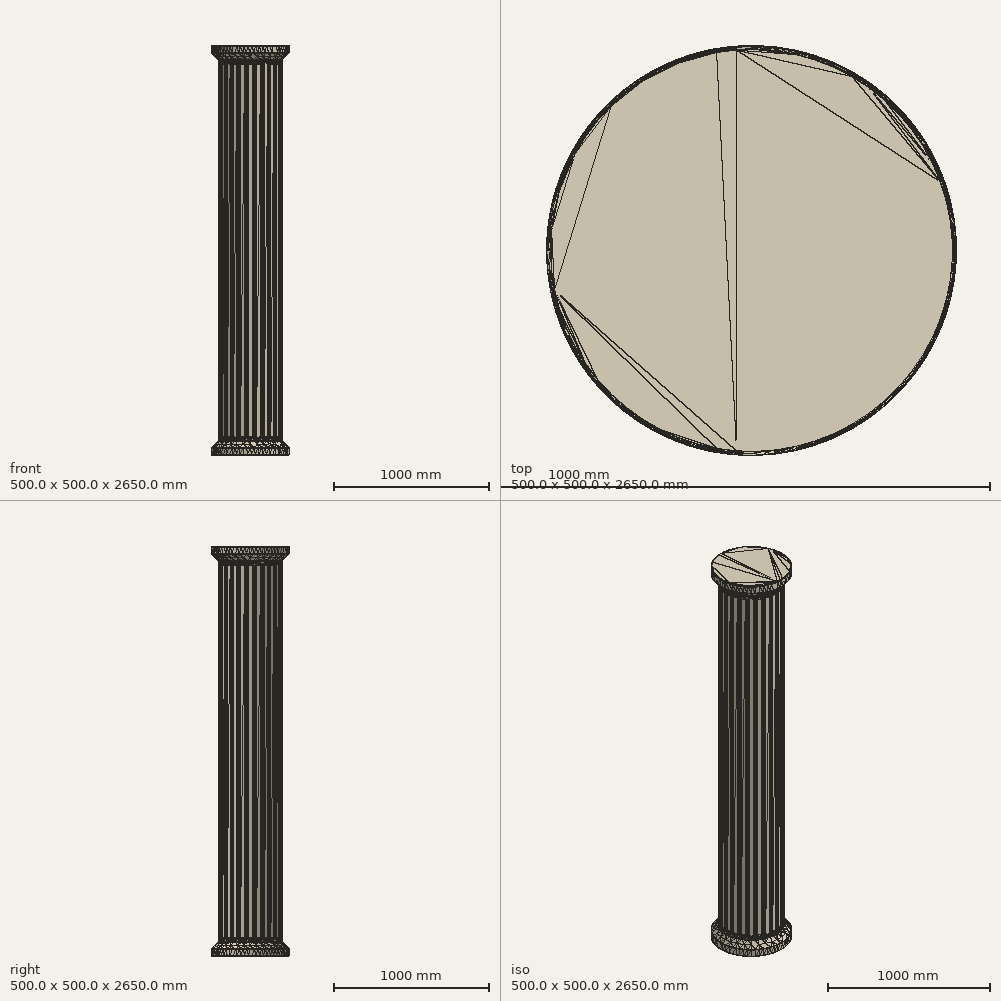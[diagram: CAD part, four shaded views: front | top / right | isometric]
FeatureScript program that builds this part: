
annotation { "Feature Type Name" : "Feature", "Feature Type Description" : "" }
export const myFeature = defineFeature(function(context is Context, id is Id, definition is map)
    precondition{}
    {
        {
            var Q0;
            Q0=qCreatedBy(makeId("Front.planeOp"),FACE);
            var sketch = newSketch(context, id + "F0", { "sketchPlane" : qUnion([Q0])});
            skLineSegment(sketch, "E0", {"start": v(0, 0) * mm, "end": v(250, 0) * mm});
            skLineSegment(sketch, "E1", {"start": v(250, 0) * mm, "end": v(250, 50) * mm});
            skLineSegment(sketch, "E2", {"start": v(250, 50) * mm, "end": v(206, 50) * mm});
            skLineSegment(sketch, "E3", {"start": v(206, 50) * mm, "end": v(206, 94) * mm});
            skLineSegment(sketch, "E4", {"start": v(206, 94) * mm, "end": v(250, 50) * mm});
            skLineSegment(sketch, "E5", {"start": v(0, 0) * mm, "end": v(0, 2650) * mm});
            skLineSegment(sketch, "E6", {"start": v(0, 2650) * mm, "end": v(250, 2650) * mm});
            skLineSegment(sketch, "E7", {"start": v(250, 2650) * mm, "end": v(250, 2600) * mm});
            skLineSegment(sketch, "E8", {"start": v(250, 2600) * mm, "end": v(206, 2600) * mm});
            skLineSegment(sketch, "E9", {"start": v(206, 2600) * mm, "end": v(206, 2556) * mm});
            skLineSegment(sketch, "E10", {"start": v(206, 2556) * mm, "end": v(250, 2600) * mm});
            skLineSegment(sketch, "E11", {"start": v(206, 2556) * mm, "end": v(206, 94) * mm});
            skLineSegment(sketch, "E12", {"start": v(206, 94) * mm, "end": v(0, 94) * mm});
            skSolve(sketch);
        }
        {
            var Q0;
            Q0 = qSketchRegion(id + "F0", true);
            var Q1;
            Q1=sQuery(id+"F0.wireOp",EDGE,"E5");
            revolve(context, id + "F1", {"surfaceOperationType" : NewSurfaceOperationType.NEW, "entities" : qUnion([Q0]), "axis" : qUnion([Q1]), "revolveType" : RevolveType.FULL});
        }
        {
            var Q0;
            Q0=qCreatedBy(makeId("Front.planeOp"),FACE);
            var sketch = newSketch(context, id + "F2", { "sketchPlane" : qUnion([Q0])});
            skLineSegment(sketch, "E13", {"start": v(0, 0) * mm, "end": v(0, 125) * mm});
            skLineSegment(sketch, "E14", {"start": v(0, 125) * mm, "end": v(10, 125) * mm});
            skLineSegment(sketch, "E15", {"start": v(10, 125) * mm, "end": v(10, 2525) * mm});
            skLineSegment(sketch, "E16", {"start": v(10, 2525) * mm, "end": v(-10, 2525) * mm});
            skLineSegment(sketch, "E17", {"start": v(-10, 2525) * mm, "end": v(-10, 125) * mm});
            skLineSegment(sketch, "E18", {"start": v(-10, 125) * mm, "end": v(0, 125) * mm});
            skArc(sketch, "E19", {"start": v(10, 2525) * mm, "mid": v(0, 2535) * mm, "end": v(-10, 2525) * mm});
            skArc(sketch, "E20", {"start": v(-10, 125) * mm, "mid": v(0, 115) * mm, "end": v(10, 125) * mm});
            skSolve(sketch);
        }
        {
            var Q0;
            Q0 = qSketchRegion(id + "F2", true);
            var Q1;
            Q1=makeQuery(id+"F1.opRevolve","SWEPT_FACE",FACE,{"disambiguationData":[OSD([sQuery(id+"F0.wireOp",EDGE,"E11")])]});
            extrude(context, id + "F3", {"entities" : qUnion([Q0]), "depth" : 210 * mm, "endBoundEntityFace" : qUnion([Q1]), "offsetDistance" : 25 * mm, "hasSecondDirection" : true, "secondDirectionOppositeDirection" : false, "secondDirectionDepth" : 200 * mm});
        }
        {
            var Q0;
            Q0=makeQuery(id+"F3.opExtrude","SWEPT_BODY",BODY,{"disambiguationData":[OSD([sQuery(id+"F2.wireOp",EDGE,"E15"),sQuery(id+"F2.wireOp",EDGE,"E17"),sQuery(id+"F2.wireOp",EDGE,"a2QfBqkh-tEiW-pIgy-MNU3-fEb1ejPm5M3t"),sQuery(id+"F2.wireOp",EDGE,"E19")])]});
            var Q1;
            Q1=sQuery(id+"F2.wireOp",EDGE,"E13");
            circularPattern(context, id + "F4", {"operationType" : NewBodyOperationType.REMOVE, "entities" : qUnion([Q0]), "axis" : qUnion([Q1]), "angle" : 360 * degree, "instanceCount" : 24, "equalSpace" : true});
        }
        {
            var Q0;
            Q0=makeQuery(id+"F4.boolean.opBoolean","INTERSECT",EDGE,{"derivedFrom":[makeQuery(id+"F1.opRevolve","SWEPT_FACE",FACE,{"disambiguationData":[OSD([sQuery(id+"F0.wireOp",EDGE,"E11")])]}),makeQuery(id+"F4.opPattern","COPY",FACE,{"derivedFrom":makeQuery(id+"F3.opExtrude","SWEPT_FACE",FACE,{"disambiguationData":[OSD([sQuery(id+"F2.wireOp",EDGE,"E17")])]}),"instanceName":"5"})]});
            var Q1;
            Q1=makeQuery(id+"F4.boolean.opBoolean","INTERSECT",EDGE,{"derivedFrom":[makeQuery(id+"F1.opRevolve","SWEPT_FACE",FACE,{"disambiguationData":[OSD([sQuery(id+"F0.wireOp",EDGE,"E11")])]}),makeQuery(id+"F4.opPattern","COPY",FACE,{"derivedFrom":makeQuery(id+"F3.opExtrude","SWEPT_FACE",FACE,{"disambiguationData":[OSD([sQuery(id+"F2.wireOp",EDGE,"E17")])]}),"instanceName":"6"})]});
            var Q2;
            Q2=makeQuery(id+"F4.boolean.opBoolean","INTERSECT",EDGE,{"derivedFrom":[makeQuery(id+"F1.opRevolve","SWEPT_FACE",FACE,{"disambiguationData":[OSD([sQuery(id+"F0.wireOp",EDGE,"E11")])]}),makeQuery(id+"F4.opPattern","COPY",FACE,{"derivedFrom":makeQuery(id+"F3.opExtrude","SWEPT_FACE",FACE,{"disambiguationData":[OSD([sQuery(id+"F2.wireOp",EDGE,"E17")])]}),"instanceName":"7"})]});
            var Q3;
            Q3=makeQuery(id+"F4.boolean.opBoolean","INTERSECT",EDGE,{"derivedFrom":[makeQuery(id+"F1.opRevolve","SWEPT_FACE",FACE,{"disambiguationData":[OSD([sQuery(id+"F0.wireOp",EDGE,"E11")])]}),makeQuery(id+"F4.opPattern","COPY",FACE,{"derivedFrom":makeQuery(id+"F3.opExtrude","SWEPT_FACE",FACE,{"disambiguationData":[OSD([sQuery(id+"F2.wireOp",EDGE,"E17")])]}),"instanceName":"8"})]});
            var Q4;
            Q4=makeQuery(id+"F4.boolean.opBoolean","INTERSECT",EDGE,{"derivedFrom":[makeQuery(id+"F1.opRevolve","SWEPT_FACE",FACE,{"disambiguationData":[OSD([sQuery(id+"F0.wireOp",EDGE,"E11")])]}),makeQuery(id+"F4.opPattern","COPY",FACE,{"derivedFrom":makeQuery(id+"F3.opExtrude","SWEPT_FACE",FACE,{"disambiguationData":[OSD([sQuery(id+"F2.wireOp",EDGE,"E17")])]}),"instanceName":"9"})]});
            var Q5;
            Q5=makeQuery(id+"F4.boolean.opBoolean","INTERSECT",EDGE,{"derivedFrom":[makeQuery(id+"F1.opRevolve","SWEPT_FACE",FACE,{"disambiguationData":[OSD([sQuery(id+"F0.wireOp",EDGE,"E11")])]}),makeQuery(id+"F4.opPattern","COPY",FACE,{"derivedFrom":makeQuery(id+"F3.opExtrude","SWEPT_FACE",FACE,{"disambiguationData":[OSD([sQuery(id+"F2.wireOp",EDGE,"E17")])]}),"instanceName":"10"})]});
            var Q6;
            Q6=makeQuery(id+"F4.boolean.opBoolean","INTERSECT",EDGE,{"derivedFrom":[makeQuery(id+"F1.opRevolve","SWEPT_FACE",FACE,{"disambiguationData":[OSD([sQuery(id+"F0.wireOp",EDGE,"E11")])]}),makeQuery(id+"F4.opPattern","COPY",FACE,{"derivedFrom":makeQuery(id+"F3.opExtrude","SWEPT_FACE",FACE,{"disambiguationData":[OSD([sQuery(id+"F2.wireOp",EDGE,"E17")])]}),"instanceName":"11"})]});
            var Q7;
            Q7=makeQuery(id+"F4.boolean.opBoolean","INTERSECT",EDGE,{"derivedFrom":[makeQuery(id+"F1.opRevolve","SWEPT_FACE",FACE,{"disambiguationData":[OSD([sQuery(id+"F0.wireOp",EDGE,"E11")])]}),makeQuery(id+"F4.opPattern","COPY",FACE,{"derivedFrom":makeQuery(id+"F3.opExtrude","SWEPT_FACE",FACE,{"disambiguationData":[OSD([sQuery(id+"F2.wireOp",EDGE,"E17")])]}),"instanceName":"12"})]});
            var Q8;
            Q8=makeQuery(id+"F4.boolean.opBoolean","INTERSECT",EDGE,{"derivedFrom":[makeQuery(id+"F1.opRevolve","SWEPT_FACE",FACE,{"disambiguationData":[OSD([sQuery(id+"F0.wireOp",EDGE,"E11")])]}),makeQuery(id+"F4.opPattern","COPY",FACE,{"derivedFrom":makeQuery(id+"F3.opExtrude","SWEPT_FACE",FACE,{"disambiguationData":[OSD([sQuery(id+"F2.wireOp",EDGE,"E17")])]}),"instanceName":"13"})]});
            var Q9;
            Q9=makeQuery(id+"F4.boolean.opBoolean","INTERSECT",EDGE,{"derivedFrom":[makeQuery(id+"F1.opRevolve","SWEPT_FACE",FACE,{"disambiguationData":[OSD([sQuery(id+"F0.wireOp",EDGE,"E11")])]}),makeQuery(id+"F4.opPattern","COPY",FACE,{"derivedFrom":makeQuery(id+"F3.opExtrude","SWEPT_FACE",FACE,{"disambiguationData":[OSD([sQuery(id+"F2.wireOp",EDGE,"E17")])]}),"instanceName":"14"})]});
            var Q10;
            Q10=makeQuery(id+"F4.boolean.opBoolean","INTERSECT",EDGE,{"derivedFrom":[makeQuery(id+"F1.opRevolve","SWEPT_FACE",FACE,{"disambiguationData":[OSD([sQuery(id+"F0.wireOp",EDGE,"E11")])]}),makeQuery(id+"F4.opPattern","COPY",FACE,{"derivedFrom":makeQuery(id+"F3.opExtrude","SWEPT_FACE",FACE,{"disambiguationData":[OSD([sQuery(id+"F2.wireOp",EDGE,"E17")])]}),"instanceName":"15"})]});
            var Q11;
            Q11=makeQuery(id+"F4.boolean.opBoolean","INTERSECT",EDGE,{"derivedFrom":[makeQuery(id+"F1.opRevolve","SWEPT_FACE",FACE,{"disambiguationData":[OSD([sQuery(id+"F0.wireOp",EDGE,"E11")])]}),makeQuery(id+"F4.opPattern","COPY",FACE,{"derivedFrom":makeQuery(id+"F3.opExtrude","SWEPT_FACE",FACE,{"disambiguationData":[OSD([sQuery(id+"F2.wireOp",EDGE,"E17")])]}),"instanceName":"16"})]});
            var Q12;
            Q12=makeQuery(id+"F4.boolean.opBoolean","INTERSECT",EDGE,{"derivedFrom":[makeQuery(id+"F1.opRevolve","SWEPT_FACE",FACE,{"disambiguationData":[OSD([sQuery(id+"F0.wireOp",EDGE,"E11")])]}),makeQuery(id+"F4.opPattern","COPY",FACE,{"derivedFrom":makeQuery(id+"F3.opExtrude","SWEPT_FACE",FACE,{"disambiguationData":[OSD([sQuery(id+"F2.wireOp",EDGE,"E17")])]}),"instanceName":"17"})]});
            var Q13;
            Q13=makeQuery(id+"F4.boolean.opBoolean","INTERSECT",EDGE,{"derivedFrom":[makeQuery(id+"F1.opRevolve","SWEPT_FACE",FACE,{"disambiguationData":[OSD([sQuery(id+"F0.wireOp",EDGE,"E11")])]}),makeQuery(id+"F4.opPattern","COPY",FACE,{"derivedFrom":makeQuery(id+"F3.opExtrude","SWEPT_FACE",FACE,{"disambiguationData":[OSD([sQuery(id+"F2.wireOp",EDGE,"E17")])]}),"instanceName":"18"})]});
            var Q14;
            Q14=makeQuery(id+"F4.boolean.opBoolean","INTERSECT",EDGE,{"derivedFrom":[makeQuery(id+"F1.opRevolve","SWEPT_FACE",FACE,{"disambiguationData":[OSD([sQuery(id+"F0.wireOp",EDGE,"E11")])]}),makeQuery(id+"F4.opPattern","COPY",FACE,{"derivedFrom":makeQuery(id+"F3.opExtrude","SWEPT_FACE",FACE,{"disambiguationData":[OSD([sQuery(id+"F2.wireOp",EDGE,"E17")])]}),"instanceName":"19"})]});
            var Q15;
            Q15=makeQuery(id+"F4.boolean.opBoolean","INTERSECT",EDGE,{"derivedFrom":[makeQuery(id+"F1.opRevolve","SWEPT_FACE",FACE,{"disambiguationData":[OSD([sQuery(id+"F0.wireOp",EDGE,"E11")])]}),makeQuery(id+"F4.opPattern","COPY",FACE,{"derivedFrom":makeQuery(id+"F3.opExtrude","SWEPT_FACE",FACE,{"disambiguationData":[OSD([sQuery(id+"F2.wireOp",EDGE,"E17")])]}),"instanceName":"20"})]});
            var Q16;
            Q16=makeQuery(id+"F4.boolean.opBoolean","INTERSECT",EDGE,{"derivedFrom":[makeQuery(id+"F1.opRevolve","SWEPT_FACE",FACE,{"disambiguationData":[OSD([sQuery(id+"F0.wireOp",EDGE,"E11")])]}),makeQuery(id+"F4.opPattern","COPY",FACE,{"derivedFrom":makeQuery(id+"F3.opExtrude","SWEPT_FACE",FACE,{"disambiguationData":[OSD([sQuery(id+"F2.wireOp",EDGE,"E17")])]}),"instanceName":"21"})]});
            var Q17;
            Q17=makeQuery(id+"F4.boolean.opBoolean","INTERSECT",EDGE,{"derivedFrom":[makeQuery(id+"F1.opRevolve","SWEPT_FACE",FACE,{"disambiguationData":[OSD([sQuery(id+"F0.wireOp",EDGE,"E11")])]}),makeQuery(id+"F4.opPattern","COPY",FACE,{"derivedFrom":makeQuery(id+"F3.opExtrude","SWEPT_FACE",FACE,{"disambiguationData":[OSD([sQuery(id+"F2.wireOp",EDGE,"E17")])]}),"instanceName":"22"})]});
            var Q18;
            Q18=makeQuery(id+"F4.boolean.opBoolean","INTERSECT",EDGE,{"derivedFrom":[makeQuery(id+"F1.opRevolve","SWEPT_FACE",FACE,{"disambiguationData":[OSD([sQuery(id+"F0.wireOp",EDGE,"E11")])]}),makeQuery(id+"F4.opPattern","COPY",FACE,{"derivedFrom":makeQuery(id+"F3.opExtrude","SWEPT_FACE",FACE,{"disambiguationData":[OSD([sQuery(id+"F2.wireOp",EDGE,"E17")])]}),"instanceName":"23"})]});
            var Q19;
            Q19=makeQuery(id+"F4.boolean.opBoolean","INTERSECT",EDGE,{"derivedFrom":[makeQuery(id+"F1.opRevolve","SWEPT_FACE",FACE,{"disambiguationData":[OSD([sQuery(id+"F0.wireOp",EDGE,"E11")])]}),makeQuery(id+"F3.opExtrude","SWEPT_FACE",FACE,{"disambiguationData":[OSD([sQuery(id+"F2.wireOp",EDGE,"E17")])]})]});
            var Q20;
            Q20=makeQuery(id+"F4.boolean.opBoolean","INTERSECT",EDGE,{"derivedFrom":[makeQuery(id+"F1.opRevolve","SWEPT_FACE",FACE,{"disambiguationData":[OSD([sQuery(id+"F0.wireOp",EDGE,"E11")])]}),makeQuery(id+"F4.opPattern","COPY",FACE,{"derivedFrom":makeQuery(id+"F3.opExtrude","SWEPT_FACE",FACE,{"disambiguationData":[OSD([sQuery(id+"F2.wireOp",EDGE,"E17")])]}),"instanceName":"1"})]});
            var Q21;
            Q21=makeQuery(id+"F4.boolean.opBoolean","INTERSECT",EDGE,{"derivedFrom":[makeQuery(id+"F1.opRevolve","SWEPT_FACE",FACE,{"disambiguationData":[OSD([sQuery(id+"F0.wireOp",EDGE,"E11")])]}),makeQuery(id+"F4.opPattern","COPY",FACE,{"derivedFrom":makeQuery(id+"F3.opExtrude","SWEPT_FACE",FACE,{"disambiguationData":[OSD([sQuery(id+"F2.wireOp",EDGE,"E17")])]}),"instanceName":"2"})]});
            var Q22;
            Q22=makeQuery(id+"F4.boolean.opBoolean","INTERSECT",EDGE,{"derivedFrom":[makeQuery(id+"F1.opRevolve","SWEPT_FACE",FACE,{"disambiguationData":[OSD([sQuery(id+"F0.wireOp",EDGE,"E11")])]}),makeQuery(id+"F4.opPattern","COPY",FACE,{"derivedFrom":makeQuery(id+"F3.opExtrude","SWEPT_FACE",FACE,{"disambiguationData":[OSD([sQuery(id+"F2.wireOp",EDGE,"E17")])]}),"instanceName":"3"})]});
            var Q23;
            Q23=makeQuery(id+"F4.boolean.opBoolean","INTERSECT",EDGE,{"derivedFrom":[makeQuery(id+"F1.opRevolve","SWEPT_FACE",FACE,{"disambiguationData":[OSD([sQuery(id+"F0.wireOp",EDGE,"E11")])]}),makeQuery(id+"F4.opPattern","COPY",FACE,{"derivedFrom":makeQuery(id+"F3.opExtrude","SWEPT_FACE",FACE,{"disambiguationData":[OSD([sQuery(id+"F2.wireOp",EDGE,"E17")])]}),"instanceName":"4"})]});
            chamfer(context, id + "F5", {"entities" : qUnion([Q0, Q1, Q2, Q3, Q4, Q5, Q6, Q7, Q8, Q9, Q10, Q11, Q12, Q13, Q14, Q15, Q16, Q17, Q18, Q19, Q20, Q21, Q22, Q23]), "width" : 10 * mm, "tangentPropagation" : true});
        }
        {
            var Q0;
            Q0=makeQuery(id+"F1.opRevolve","SWEPT_EDGE",EDGE,{"disambiguationData":[OSD([sQuery(id+"F0.wireOp",EDGE,"E6"),sQuery(id+"F0.wireOp",EDGE,"E7")])]});
            var Q1;
            Q1=makeQuery(id+"F1.opRevolve","SWEPT_EDGE",EDGE,{"disambiguationData":[OSD([sQuery(id+"F0.wireOp",EDGE,"E7"),sQuery(id+"F0.wireOp",EDGE,"E8"),sQuery(id+"F0.wireOp",EDGE,"E10")])]});
            var Q2;
            Q2=makeQuery(id+"F1.opRevolve","SWEPT_EDGE",EDGE,{"disambiguationData":[OSD([sQuery(id+"F0.wireOp",EDGE,"E9"),sQuery(id+"F0.wireOp",EDGE,"E10"),sQuery(id+"F0.wireOp",EDGE,"E11")])]});
            var Q3;
            Q3=makeQuery(id+"F1.opRevolve","SWEPT_EDGE",EDGE,{"disambiguationData":[OSD([sQuery(id+"F0.wireOp",EDGE,"E0"),sQuery(id+"F0.wireOp",EDGE,"E1")])]});
            var Q4;
            Q4=makeQuery(id+"F1.opRevolve","SWEPT_EDGE",EDGE,{"disambiguationData":[OSD([sQuery(id+"F0.wireOp",EDGE,"E1"),sQuery(id+"F0.wireOp",EDGE,"E2"),sQuery(id+"F0.wireOp",EDGE,"E4")])]});
            var Q5;
            Q5=makeQuery(id+"F1.opRevolve","SWEPT_EDGE",EDGE,{"disambiguationData":[OSD([sQuery(id+"F0.wireOp",EDGE,"E3"),sQuery(id+"F0.wireOp",EDGE,"E4"),sQuery(id+"F0.wireOp",EDGE,"E11"),sQuery(id+"F0.wireOp",EDGE,"E12")])]});
            var Q6;
            Q6=makeQuery(id+"F4.boolean.opBoolean","COPY",FACE,{"derivedFrom":makeQuery(id+"F4.opPattern","COPY",FACE,{"derivedFrom":makeQuery(id+"F3.opExtrude","CAP_FACE",FACE,{"disambiguationData":[OSD([sQuery(id+"F2.wireOp",EDGE,"E15"),sQuery(id+"F2.wireOp",EDGE,"E17"),sQuery(id+"F2.wireOp",EDGE,"E19"),sQuery(id+"F2.wireOp",EDGE,"E20")])],"isStart":true}),"instanceName":"3"})});
            var Q7;
            Q7=makeQuery(id+"F4.boolean.opBoolean","COPY",FACE,{"derivedFrom":makeQuery(id+"F4.opPattern","COPY",FACE,{"derivedFrom":makeQuery(id+"F3.opExtrude","CAP_FACE",FACE,{"disambiguationData":[OSD([sQuery(id+"F2.wireOp",EDGE,"E15"),sQuery(id+"F2.wireOp",EDGE,"E17"),sQuery(id+"F2.wireOp",EDGE,"E19"),sQuery(id+"F2.wireOp",EDGE,"E20")])],"isStart":true}),"instanceName":"4"})});
            var Q8;
            Q8=makeQuery(id+"F4.boolean.opBoolean","COPY",FACE,{"derivedFrom":makeQuery(id+"F4.opPattern","COPY",FACE,{"derivedFrom":makeQuery(id+"F3.opExtrude","CAP_FACE",FACE,{"disambiguationData":[OSD([sQuery(id+"F2.wireOp",EDGE,"E15"),sQuery(id+"F2.wireOp",EDGE,"E17"),sQuery(id+"F2.wireOp",EDGE,"E19"),sQuery(id+"F2.wireOp",EDGE,"E20")])],"isStart":true}),"instanceName":"5"})});
            var Q9;
            Q9=makeQuery(id+"F4.boolean.opBoolean","COPY",FACE,{"derivedFrom":makeQuery(id+"F4.opPattern","COPY",FACE,{"derivedFrom":makeQuery(id+"F3.opExtrude","CAP_FACE",FACE,{"disambiguationData":[OSD([sQuery(id+"F2.wireOp",EDGE,"E15"),sQuery(id+"F2.wireOp",EDGE,"E17"),sQuery(id+"F2.wireOp",EDGE,"E19"),sQuery(id+"F2.wireOp",EDGE,"E20")])],"isStart":true}),"instanceName":"6"})});
            var Q10;
            Q10=makeQuery(id+"F4.boolean.opBoolean","COPY",FACE,{"derivedFrom":makeQuery(id+"F4.opPattern","COPY",FACE,{"derivedFrom":makeQuery(id+"F3.opExtrude","CAP_FACE",FACE,{"disambiguationData":[OSD([sQuery(id+"F2.wireOp",EDGE,"E15"),sQuery(id+"F2.wireOp",EDGE,"E17"),sQuery(id+"F2.wireOp",EDGE,"E19"),sQuery(id+"F2.wireOp",EDGE,"E20")])],"isStart":true}),"instanceName":"7"})});
            var Q11;
            Q11=makeQuery(id+"F4.boolean.opBoolean","COPY",FACE,{"derivedFrom":makeQuery(id+"F4.opPattern","COPY",FACE,{"derivedFrom":makeQuery(id+"F3.opExtrude","CAP_FACE",FACE,{"disambiguationData":[OSD([sQuery(id+"F2.wireOp",EDGE,"E15"),sQuery(id+"F2.wireOp",EDGE,"E17"),sQuery(id+"F2.wireOp",EDGE,"E19"),sQuery(id+"F2.wireOp",EDGE,"E20")])],"isStart":true}),"instanceName":"8"})});
            var Q12;
            Q12=makeQuery(id+"F4.boolean.opBoolean","COPY",FACE,{"derivedFrom":makeQuery(id+"F4.opPattern","COPY",FACE,{"derivedFrom":makeQuery(id+"F3.opExtrude","CAP_FACE",FACE,{"disambiguationData":[OSD([sQuery(id+"F2.wireOp",EDGE,"E15"),sQuery(id+"F2.wireOp",EDGE,"E17"),sQuery(id+"F2.wireOp",EDGE,"E19"),sQuery(id+"F2.wireOp",EDGE,"E20")])],"isStart":true}),"instanceName":"9"})});
            var Q13;
            Q13=makeQuery(id+"F4.boolean.opBoolean","COPY",FACE,{"derivedFrom":makeQuery(id+"F4.opPattern","COPY",FACE,{"derivedFrom":makeQuery(id+"F3.opExtrude","CAP_FACE",FACE,{"disambiguationData":[OSD([sQuery(id+"F2.wireOp",EDGE,"E15"),sQuery(id+"F2.wireOp",EDGE,"E17"),sQuery(id+"F2.wireOp",EDGE,"E19"),sQuery(id+"F2.wireOp",EDGE,"E20")])],"isStart":true}),"instanceName":"10"})});
            var Q14;
            Q14=makeQuery(id+"F4.boolean.opBoolean","COPY",FACE,{"derivedFrom":makeQuery(id+"F4.opPattern","COPY",FACE,{"derivedFrom":makeQuery(id+"F3.opExtrude","CAP_FACE",FACE,{"disambiguationData":[OSD([sQuery(id+"F2.wireOp",EDGE,"E15"),sQuery(id+"F2.wireOp",EDGE,"E17"),sQuery(id+"F2.wireOp",EDGE,"E19"),sQuery(id+"F2.wireOp",EDGE,"E20")])],"isStart":true}),"instanceName":"11"})});
            var Q15;
            Q15=makeQuery(id+"F4.boolean.opBoolean","COPY",FACE,{"derivedFrom":makeQuery(id+"F4.opPattern","COPY",FACE,{"derivedFrom":makeQuery(id+"F3.opExtrude","CAP_FACE",FACE,{"disambiguationData":[OSD([sQuery(id+"F2.wireOp",EDGE,"E15"),sQuery(id+"F2.wireOp",EDGE,"E17"),sQuery(id+"F2.wireOp",EDGE,"E19"),sQuery(id+"F2.wireOp",EDGE,"E20")])],"isStart":true}),"instanceName":"12"})});
            var Q16;
            Q16=makeQuery(id+"F4.boolean.opBoolean","COPY",FACE,{"derivedFrom":makeQuery(id+"F4.opPattern","COPY",FACE,{"derivedFrom":makeQuery(id+"F3.opExtrude","CAP_FACE",FACE,{"disambiguationData":[OSD([sQuery(id+"F2.wireOp",EDGE,"E15"),sQuery(id+"F2.wireOp",EDGE,"E17"),sQuery(id+"F2.wireOp",EDGE,"E19"),sQuery(id+"F2.wireOp",EDGE,"E20")])],"isStart":true}),"instanceName":"13"})});
            var Q17;
            Q17=makeQuery(id+"F4.boolean.opBoolean","COPY",FACE,{"derivedFrom":makeQuery(id+"F4.opPattern","COPY",FACE,{"derivedFrom":makeQuery(id+"F3.opExtrude","CAP_FACE",FACE,{"disambiguationData":[OSD([sQuery(id+"F2.wireOp",EDGE,"E15"),sQuery(id+"F2.wireOp",EDGE,"E17"),sQuery(id+"F2.wireOp",EDGE,"E19"),sQuery(id+"F2.wireOp",EDGE,"E20")])],"isStart":true}),"instanceName":"14"})});
            var Q18;
            Q18=makeQuery(id+"F4.boolean.opBoolean","COPY",FACE,{"derivedFrom":makeQuery(id+"F4.opPattern","COPY",FACE,{"derivedFrom":makeQuery(id+"F3.opExtrude","CAP_FACE",FACE,{"disambiguationData":[OSD([sQuery(id+"F2.wireOp",EDGE,"E15"),sQuery(id+"F2.wireOp",EDGE,"E17"),sQuery(id+"F2.wireOp",EDGE,"E19"),sQuery(id+"F2.wireOp",EDGE,"E20")])],"isStart":true}),"instanceName":"15"})});
            var Q19;
            Q19=makeQuery(id+"F4.boolean.opBoolean","COPY",FACE,{"derivedFrom":makeQuery(id+"F4.opPattern","COPY",FACE,{"derivedFrom":makeQuery(id+"F3.opExtrude","CAP_FACE",FACE,{"disambiguationData":[OSD([sQuery(id+"F2.wireOp",EDGE,"E15"),sQuery(id+"F2.wireOp",EDGE,"E17"),sQuery(id+"F2.wireOp",EDGE,"E19"),sQuery(id+"F2.wireOp",EDGE,"E20")])],"isStart":true}),"instanceName":"16"})});
            var Q20;
            Q20=makeQuery(id+"F4.boolean.opBoolean","COPY",FACE,{"derivedFrom":makeQuery(id+"F4.opPattern","COPY",FACE,{"derivedFrom":makeQuery(id+"F3.opExtrude","CAP_FACE",FACE,{"disambiguationData":[OSD([sQuery(id+"F2.wireOp",EDGE,"E15"),sQuery(id+"F2.wireOp",EDGE,"E17"),sQuery(id+"F2.wireOp",EDGE,"E19"),sQuery(id+"F2.wireOp",EDGE,"E20")])],"isStart":true}),"instanceName":"17"})});
            var Q21;
            Q21=makeQuery(id+"F4.boolean.opBoolean","COPY",FACE,{"derivedFrom":makeQuery(id+"F4.opPattern","COPY",FACE,{"derivedFrom":makeQuery(id+"F3.opExtrude","CAP_FACE",FACE,{"disambiguationData":[OSD([sQuery(id+"F2.wireOp",EDGE,"E15"),sQuery(id+"F2.wireOp",EDGE,"E17"),sQuery(id+"F2.wireOp",EDGE,"E19"),sQuery(id+"F2.wireOp",EDGE,"E20")])],"isStart":true}),"instanceName":"18"})});
            var Q22;
            Q22=makeQuery(id+"F4.boolean.opBoolean","COPY",FACE,{"derivedFrom":makeQuery(id+"F4.opPattern","COPY",FACE,{"derivedFrom":makeQuery(id+"F3.opExtrude","CAP_FACE",FACE,{"disambiguationData":[OSD([sQuery(id+"F2.wireOp",EDGE,"E15"),sQuery(id+"F2.wireOp",EDGE,"E17"),sQuery(id+"F2.wireOp",EDGE,"E19"),sQuery(id+"F2.wireOp",EDGE,"E20")])],"isStart":true}),"instanceName":"19"})});
            var Q23;
            Q23=makeQuery(id+"F4.boolean.opBoolean","COPY",FACE,{"derivedFrom":makeQuery(id+"F4.opPattern","COPY",FACE,{"derivedFrom":makeQuery(id+"F3.opExtrude","CAP_FACE",FACE,{"disambiguationData":[OSD([sQuery(id+"F2.wireOp",EDGE,"E15"),sQuery(id+"F2.wireOp",EDGE,"E17"),sQuery(id+"F2.wireOp",EDGE,"E19"),sQuery(id+"F2.wireOp",EDGE,"E20")])],"isStart":true}),"instanceName":"20"})});
            var Q24;
            Q24=makeQuery(id+"F4.boolean.opBoolean","COPY",FACE,{"derivedFrom":makeQuery(id+"F4.opPattern","COPY",FACE,{"derivedFrom":makeQuery(id+"F3.opExtrude","CAP_FACE",FACE,{"disambiguationData":[OSD([sQuery(id+"F2.wireOp",EDGE,"E15"),sQuery(id+"F2.wireOp",EDGE,"E17"),sQuery(id+"F2.wireOp",EDGE,"E19"),sQuery(id+"F2.wireOp",EDGE,"E20")])],"isStart":true}),"instanceName":"21"})});
            var Q25;
            Q25=makeQuery(id+"F4.boolean.opBoolean","COPY",FACE,{"derivedFrom":makeQuery(id+"F4.opPattern","COPY",FACE,{"derivedFrom":makeQuery(id+"F3.opExtrude","CAP_FACE",FACE,{"disambiguationData":[OSD([sQuery(id+"F2.wireOp",EDGE,"E15"),sQuery(id+"F2.wireOp",EDGE,"E17"),sQuery(id+"F2.wireOp",EDGE,"E19"),sQuery(id+"F2.wireOp",EDGE,"E20")])],"isStart":true}),"instanceName":"22"})});
            var Q26;
            Q26=makeQuery(id+"F4.boolean.opBoolean","COPY",FACE,{"derivedFrom":makeQuery(id+"F4.opPattern","COPY",FACE,{"derivedFrom":makeQuery(id+"F3.opExtrude","CAP_FACE",FACE,{"disambiguationData":[OSD([sQuery(id+"F2.wireOp",EDGE,"E15"),sQuery(id+"F2.wireOp",EDGE,"E17"),sQuery(id+"F2.wireOp",EDGE,"E19"),sQuery(id+"F2.wireOp",EDGE,"E20")])],"isStart":true}),"instanceName":"23"})});
            var Q27;
            Q27=makeQuery(id+"F4.boolean.opBoolean","COPY",FACE,{"derivedFrom":makeQuery(id+"F3.opExtrude","CAP_FACE",FACE,{"disambiguationData":[OSD([sQuery(id+"F2.wireOp",EDGE,"E15"),sQuery(id+"F2.wireOp",EDGE,"E17"),sQuery(id+"F2.wireOp",EDGE,"E19"),sQuery(id+"F2.wireOp",EDGE,"E20")])],"isStart":true})});
            var Q28;
            Q28=makeQuery(id+"F4.boolean.opBoolean","COPY",FACE,{"derivedFrom":makeQuery(id+"F4.opPattern","COPY",FACE,{"derivedFrom":makeQuery(id+"F3.opExtrude","CAP_FACE",FACE,{"disambiguationData":[OSD([sQuery(id+"F2.wireOp",EDGE,"E15"),sQuery(id+"F2.wireOp",EDGE,"E17"),sQuery(id+"F2.wireOp",EDGE,"E19"),sQuery(id+"F2.wireOp",EDGE,"E20")])],"isStart":true}),"instanceName":"1"})});
            var Q29;
            Q29=makeQuery(id+"F4.boolean.opBoolean","COPY",FACE,{"derivedFrom":makeQuery(id+"F4.opPattern","COPY",FACE,{"derivedFrom":makeQuery(id+"F3.opExtrude","CAP_FACE",FACE,{"disambiguationData":[OSD([sQuery(id+"F2.wireOp",EDGE,"E15"),sQuery(id+"F2.wireOp",EDGE,"E17"),sQuery(id+"F2.wireOp",EDGE,"E19"),sQuery(id+"F2.wireOp",EDGE,"E20")])],"isStart":true}),"instanceName":"2"})});
            fillet(context, id + "F6", {"entities" : qUnion([Q0, Q1, Q2, Q3, Q4, Q5, Q6, Q7, Q8, Q9, Q10, Q11, Q12, Q13, Q14, Q15, Q16, Q17, Q18, Q19, Q20, Q21, Q22, Q23, Q24, Q25, Q26, Q27, Q28, Q29]), "radius" : 5 * mm, "tangentPropagation" : true, "allowEdgeOverflow" : false});
        }
        {
            var Q0;
            Q0=makeQuery(id+"F1.opRevolve","SWEPT_FACE",FACE,{"disambiguationData":[OSD([sQuery(id+"F0.wireOp",EDGE,"E11")])]});
            fillet(context, id + "F7", {"entities" : qUnion([Q0]), "radius" : 5 * mm, "tangentPropagation" : true, "allowEdgeOverflow" : false});
        }
    });
